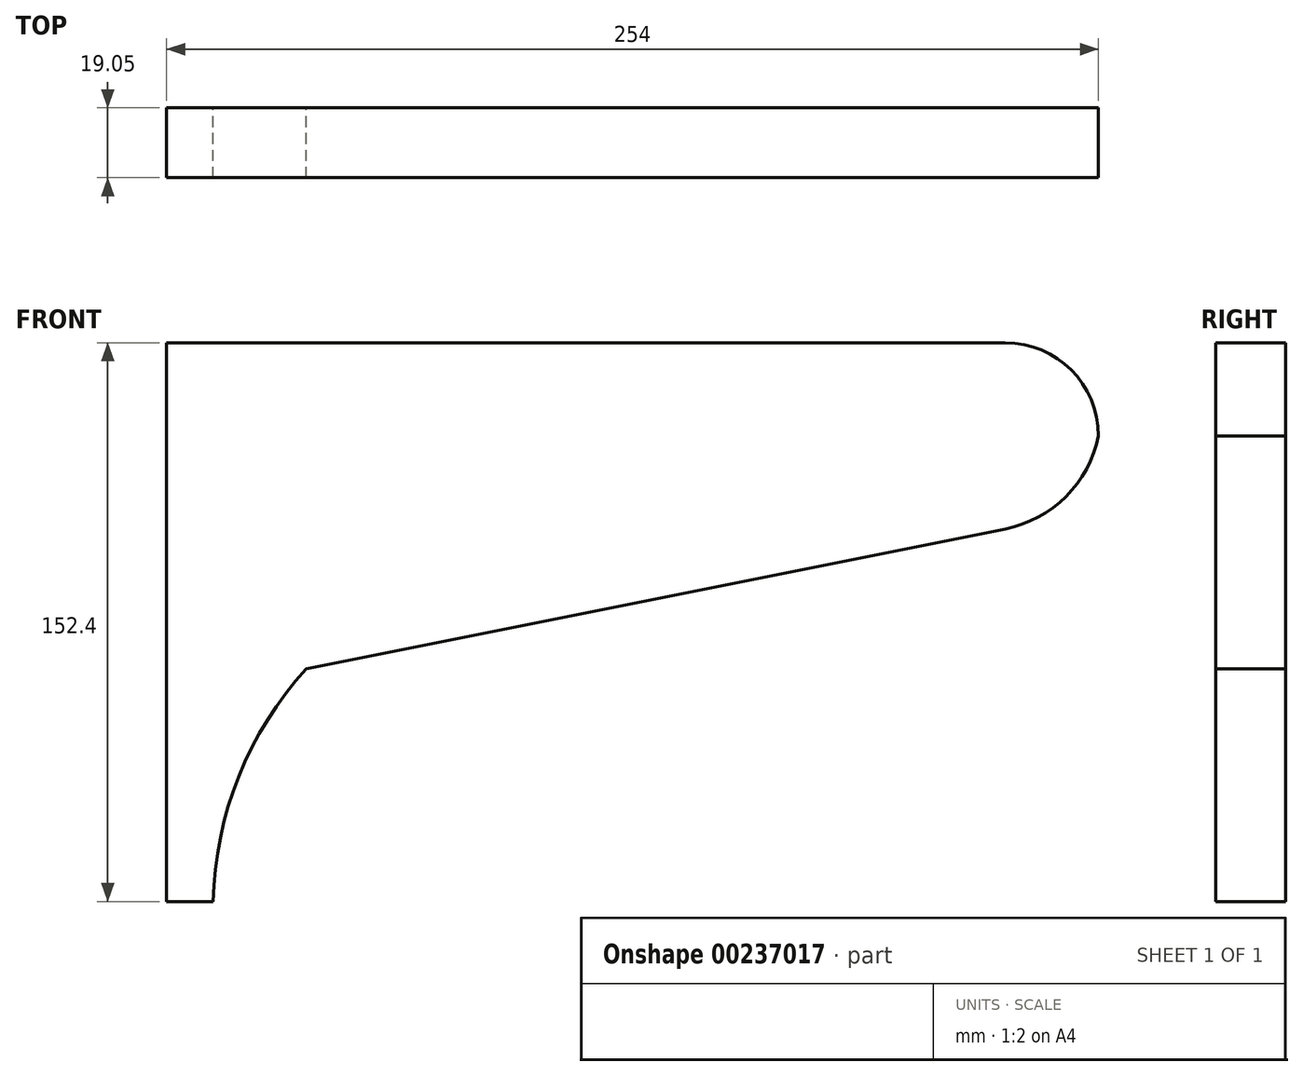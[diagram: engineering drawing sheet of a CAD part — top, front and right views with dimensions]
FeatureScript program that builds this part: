
annotation { "Feature Type Name" : "Feature", "Feature Type Description" : "" }
export const myFeature = defineFeature(function(context is Context, id is Id, definition is map)
    precondition{}
    {
        {
            var Q0;
            Q0=qCreatedBy(makeId("Front.planeOp"),FACE);
            var sketch = newSketch(context, id + "F0", { "sketchPlane" : qUnion([Q0])});
            skLineSegment(sketch, "E0.right", {"start": v(-127, 76.2) * mm, "end": v(-127, -76.2) * mm});
            skPoint(sketch, "E0.middle", {"position": v(0, 0) * mm});
            skLineSegment(sketch, "E1", {"start": v(-127, 76.2) * mm, "end": v(101.6, 76.2) * mm});
            skArc(sketch, "E2", {"start": v(127, 50.8) * mm, "mid": v(119.56, 68.76) * mm, "end": v(101.6, 76.2) * mm});
            skLineSegment(sketch, "E3", {"start": v(-127, -76.2) * mm, "end": v(-114.3, -76.2) * mm});
            skArc(sketch, "E4", {"start": v(-88.9, -12.7) * mm, "mid": v(-107.35, -42.15) * mm, "end": v(-114.3, -76.2) * mm});
            skLineSegment(sketch, "E5", {"start": v(-88.9, -12.7) * mm, "end": v(101.6, 25.4) * mm});
            skArc(sketch, "E6", {"start": v(101.6, 25.4) * mm, "mid": v(118.15, 34.25) * mm, "end": v(127, 50.8) * mm});
            skSolve(sketch);
        }
        {
            var Q0;
            Q0=makeQuery(id+"F0.imprint","IMPRINT",FACE,{"disambiguationData":[TD([[makeQuery(id+"F0.imprint","IMPRINT",EDGE,{"derivedFrom":sQuery(id+"F0.wireOp",EDGE,"E0.right")}),1.0]])]});
            extrude(context, id + "F1", {"entities" : qUnion([Q0]), "depth" : 19.05 * mm});
        }
    });
